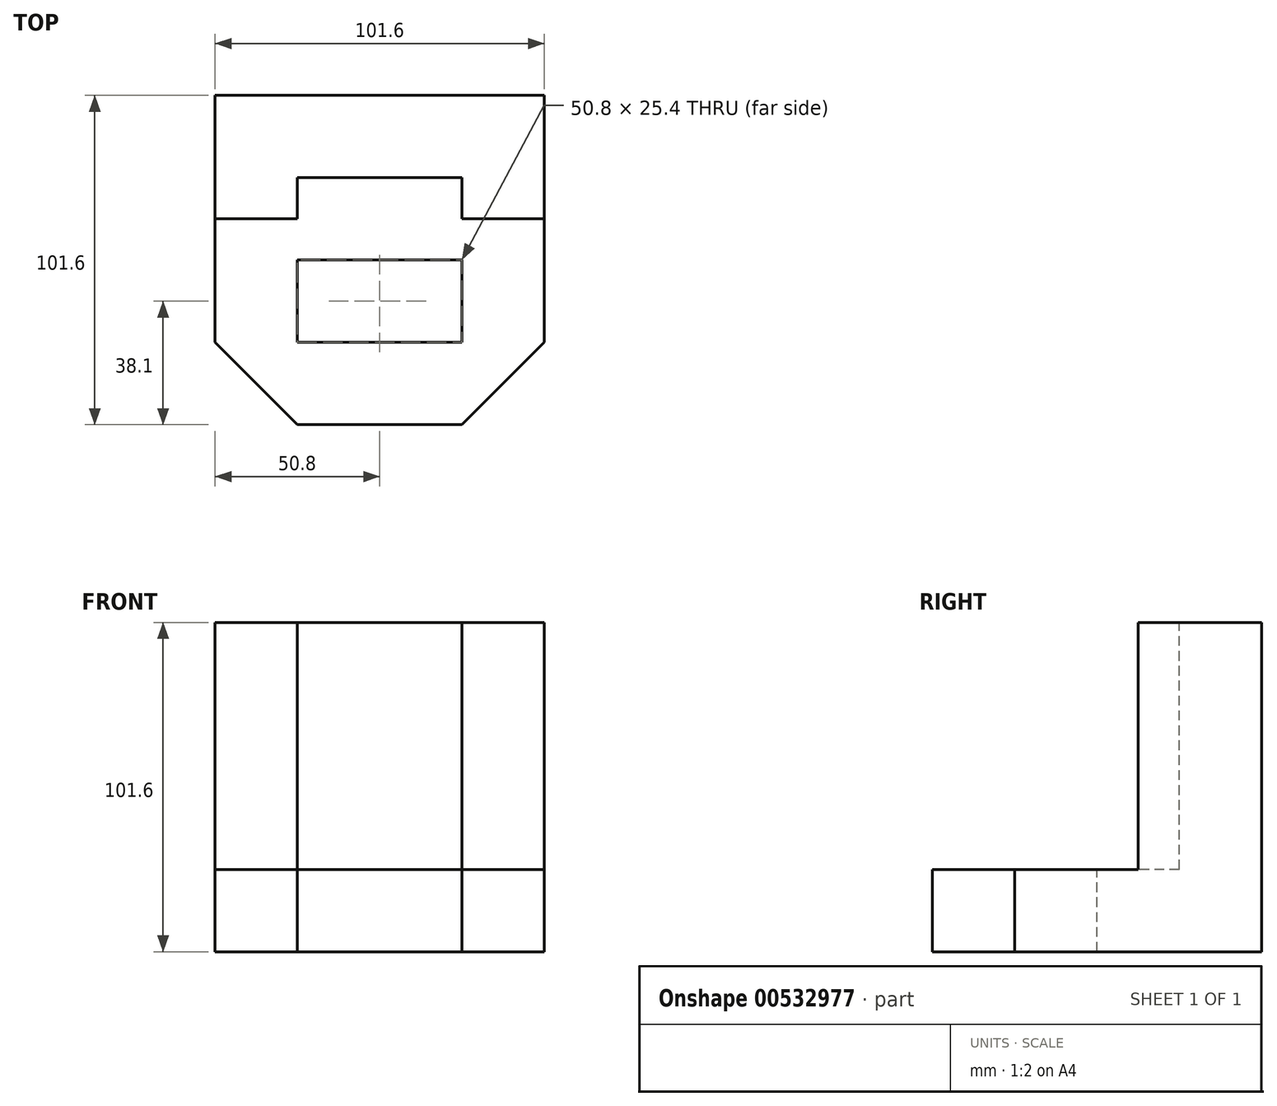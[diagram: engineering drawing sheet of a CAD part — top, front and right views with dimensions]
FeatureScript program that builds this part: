
annotation { "Feature Type Name" : "Feature", "Feature Type Description" : "" }
export const myFeature = defineFeature(function(context is Context, id is Id, definition is map)
    precondition{}
    {
        {
            var Q0;
            Q0=qCreatedBy(makeId("Front.planeOp"),FACE);
            var sketch = newSketch(context, id + "F0", { "sketchPlane" : qUnion([Q0])});
            skLineSegment(sketch, "E0.bottom", {"start": v(-101.6, 83.23) * mm, "end": v(0, 83.23) * mm});
            skLineSegment(sketch, "E0.top", {"start": v(-101.6, -18.37) * mm, "end": v(0, -18.37) * mm});
            skLineSegment(sketch, "E0.left", {"start": v(-101.6, 83.23) * mm, "end": v(-101.6, -18.37) * mm});
            skLineSegment(sketch, "E0.right", {"start": v(0, 83.23) * mm, "end": v(0, -18.37) * mm});
            skSolve(sketch);
        }
        {
            var Q0;
            Q0=makeQuery(id+"F0.imprint","IMPRINT",FACE,{"disambiguationData":[TD([[makeQuery(id+"F0.imprint","IMPRINT",EDGE,{"derivedFrom":sQuery(id+"F0.wireOp",EDGE,"E0.bottom")}),-1.0]])]});
            extrude(context, id + "F1", {"entities" : qUnion([Q0]), "depth" : 101.6 * mm, "offsetDistance" : 25.4 * mm});
        }
        {
            var Q0;
            Q0=makeQuery(id+"F1.opExtrude","SWEPT_FACE",FACE,{"disambiguationData":[OSD([sQuery(id+"F0.wireOp",EDGE,"E0.bottom")])]});
            var sketch = newSketch(context, id + "F2", { "sketchPlane" : qUnion([Q0])});
            skLineSegment(sketch, "E1", {"start": v(-101.6, 0) * mm, "end": v(-101.6, -38.1) * mm});
            skLineSegment(sketch, "E2", {"start": v(-101.6, -38.1) * mm, "end": v(-76.2, -38.1) * mm});
            skLineSegment(sketch, "E3", {"start": v(-76.2, -38.1) * mm, "end": v(-76.2, -25.4) * mm});
            skLineSegment(sketch, "E4", {"start": v(-76.2, -25.4) * mm, "end": v(-25.4, -25.4) * mm});
            skLineSegment(sketch, "E5", {"start": v(-25.4, -25.4) * mm, "end": v(-25.4, -38.1) * mm});
            skLineSegment(sketch, "E6", {"start": v(-25.4, -38.1) * mm, "end": v(0, -38.1) * mm});
            skLineSegment(sketch, "E7", {"start": v(0, -38.1) * mm, "end": v(0, 0) * mm});
            skLineSegment(sketch, "E8", {"start": v(0, 0) * mm, "end": v(-101.6, 0) * mm});
            skSolve(sketch);
        }
        {
            var Q0;
            {var subQ0=sQuery(id+"F2.wireOp",EDGE,"E2");Q0=makeQuery(id+"F2.imprint","IMPRINT",FACE,{"disambiguationData":[TD([[makeQuery(id+"F2.imprint","IMPRINT",EDGE,{"derivedFrom":subQ0}),-1.0]])]});}
            extrude(context, id + "F3", {"entities" : qUnion([Q0]), "operationType" : NewBodyOperationType.REMOVE, "oppositeDirection" : true, "depth" : 76.2 * mm, "offsetDistance" : 25.4 * mm});
        }
        {
            var Q0;
            Q0=makeQuery(id+"F3.boolean.opBoolean","COPY",FACE,{"derivedFrom":makeQuery(id+"F3.opExtrude","CAP_FACE",FACE,{"disambiguationData":[OSD([sQuery(id+"F0.wireOp",EDGE,"E0.bottom"),sQuery(id+"F0.wireOp",EDGE,"E0.left"),sQuery(id+"F0.wireOp",EDGE,"E0.right"),sQuery(id+"F2.wireOp",EDGE,"E2"),sQuery(id+"F2.wireOp",EDGE,"E3"),sQuery(id+"F2.wireOp",EDGE,"E4"),sQuery(id+"F2.wireOp",EDGE,"E5"),sQuery(id+"F2.wireOp",EDGE,"E6")])],"isStart":false})});
            var sketch = newSketch(context, id + "F4", { "sketchPlane" : qUnion([Q0])});
            skLineSegment(sketch, "E9", {"start": v(-101.6, -38.1) * mm, "end": v(-101.6, -76.2) * mm});
            skLineSegment(sketch, "E10", {"start": v(-101.6, -101.6) * mm, "end": v(-76.2, -101.6) * mm});
            skLineSegment(sketch, "E11", {"start": v(0, -101.6) * mm, "end": v(-25.4, -101.6) * mm});
            skLineSegment(sketch, "E12", {"start": v(0, -38.1) * mm, "end": v(0, -76.2) * mm});
            skLineSegment(sketch, "E13", {"start": v(0, -76.2) * mm, "end": v(-25.4, -101.6) * mm});
            skLineSegment(sketch, "E14", {"start": v(-101.6, -76.2) * mm, "end": v(-76.2, -101.6) * mm});
            skSolve(sketch);
        }
        {
            var Q0;
            {var subQ0=sQuery(id+"F4.wireOp",EDGE,"E10");Q0=makeQuery(id+"F4.imprint","IMPRINT",FACE,{"disambiguationData":[TD([[makeQuery(id+"F4.imprint","IMPRINT",EDGE,{"derivedFrom":subQ0}),1.0]])]});}
            var Q1;
            {var subQ0=sQuery(id+"F4.wireOp",EDGE,"E11");Q1=makeQuery(id+"F4.imprint","IMPRINT",FACE,{"disambiguationData":[TD([[makeQuery(id+"F4.imprint","IMPRINT",EDGE,{"derivedFrom":subQ0}),1.0]])]});}
            extrude(context, id + "F5", {"entities" : qUnion([Q0, Q1]), "operationType" : NewBodyOperationType.REMOVE, "oppositeDirection" : true, "depth" : 87.38 * mm, "offsetDistance" : 25.4 * mm});
        }
        {
            var Q0;
            Q0=makeQuery(id+"F3.boolean.opBoolean","COPY",FACE,{"derivedFrom":makeQuery(id+"F3.opExtrude","CAP_FACE",FACE,{"disambiguationData":[OSD([sQuery(id+"F0.wireOp",EDGE,"E0.bottom"),sQuery(id+"F0.wireOp",EDGE,"E0.left"),sQuery(id+"F0.wireOp",EDGE,"E0.right"),sQuery(id+"F2.wireOp",EDGE,"E2"),sQuery(id+"F2.wireOp",EDGE,"E3"),sQuery(id+"F2.wireOp",EDGE,"E4"),sQuery(id+"F2.wireOp",EDGE,"E5"),sQuery(id+"F2.wireOp",EDGE,"E6")])],"isStart":false})});
            var sketch = newSketch(context, id + "F6", { "sketchPlane" : qUnion([Q0])});
            skLineSegment(sketch, "E15", {"start": v(-76.2, -38.1) * mm, "end": v(-76.2, -50.8) * mm});
            skLineSegment(sketch, "E16", {"start": v(-76.2, -50.8) * mm, "end": v(-25.4, -50.8) * mm});
            skLineSegment(sketch, "E17", {"start": v(-25.4, -50.8) * mm, "end": v(-25.4, -38.1) * mm});
            skLineSegment(sketch, "E18", {"start": v(-76.2, -50.8) * mm, "end": v(-76.2, -101.6) * mm});
            skLineSegment(sketch, "E19", {"start": v(-25.4, -50.8) * mm, "end": v(-25.4, -101.6) * mm});
            skLineSegment(sketch, "E20", {"start": v(-76.2, -50.8) * mm, "end": v(-63.5, -50.8) * mm});
            skLineSegment(sketch, "E21", {"start": v(-25.4, -50.8) * mm, "end": v(-38.1, -50.8) * mm});
            skLineSegment(sketch, "E22", {"start": v(-25.4, -50.8) * mm, "end": v(-25.4, -76.2) * mm});
            skLineSegment(sketch, "E23", {"start": v(-76.2, -50.8) * mm, "end": v(-76.2, -76.2) * mm});
            skLineSegment(sketch, "E24", {"start": v(-76.2, -76.2) * mm, "end": v(-25.4, -76.2) * mm});
            skLineSegment(sketch, "E25", {"start": v(-38.1, -50.8) * mm, "end": v(-38.1, -76.2) * mm});
            skLineSegment(sketch, "E26", {"start": v(-63.5, -50.8) * mm, "end": v(-63.5, -76.2) * mm});
            skSolve(sketch);
        }
        {
            var Q0;
            Q0=makeQuery(id+"F6.imprint","IMPRINT",FACE,{"disambiguationData":[TD([[makeQuery(id+"F6.imprint","IMPRINT",EDGE,{"derivedFrom":sQuery(id+"F6.wireOp",EDGE,"E16")}),-1.0]])]});
            extrude(context, id + "F7", {"entities" : qUnion([Q0]), "operationType" : NewBodyOperationType.REMOVE, "oppositeDirection" : true, "depth" : 103.38 * mm, "offsetDistance" : 25.4 * mm});
        }
    });
